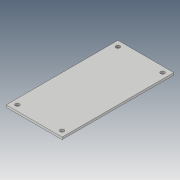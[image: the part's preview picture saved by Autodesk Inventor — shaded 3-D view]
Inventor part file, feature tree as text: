
AUTODESK INVENTOR PART (.ipt)
format: ipt  version: 2019 (Build 230136000, 136)  size: 97,792 bytes
history: native  units: mm
features: extrude x2, sketch x2
ambient origin geometry x8: Origin, YZ Plane, XZ Plane, XY Plane, X Axis, Y Axis, Z Axis, Center Point
bodies: Solid1 (feature_tree)
feature tree (4):
  extrude  "Extrusion1"  Depth=50.0mm
  extrude  "Extrusion2"  Depth=2.0mm
  sketch  "Sketch1"  dims[d0=100.0mm d1=50.0mm]
  sketch  "Sketch2"  dims[d2=2.0mm d3=0.0mm d4=3.5mm d5=5.0mm d6=5.0mm d7=3.5mm d8=3.5mm d9=3.5mm d10=5.0mm d11=5.0mm d12=5.0mm d13=5.0mm d14=5.0mm d15=5.0mm d16=2.0mm d17=0.0mm]
